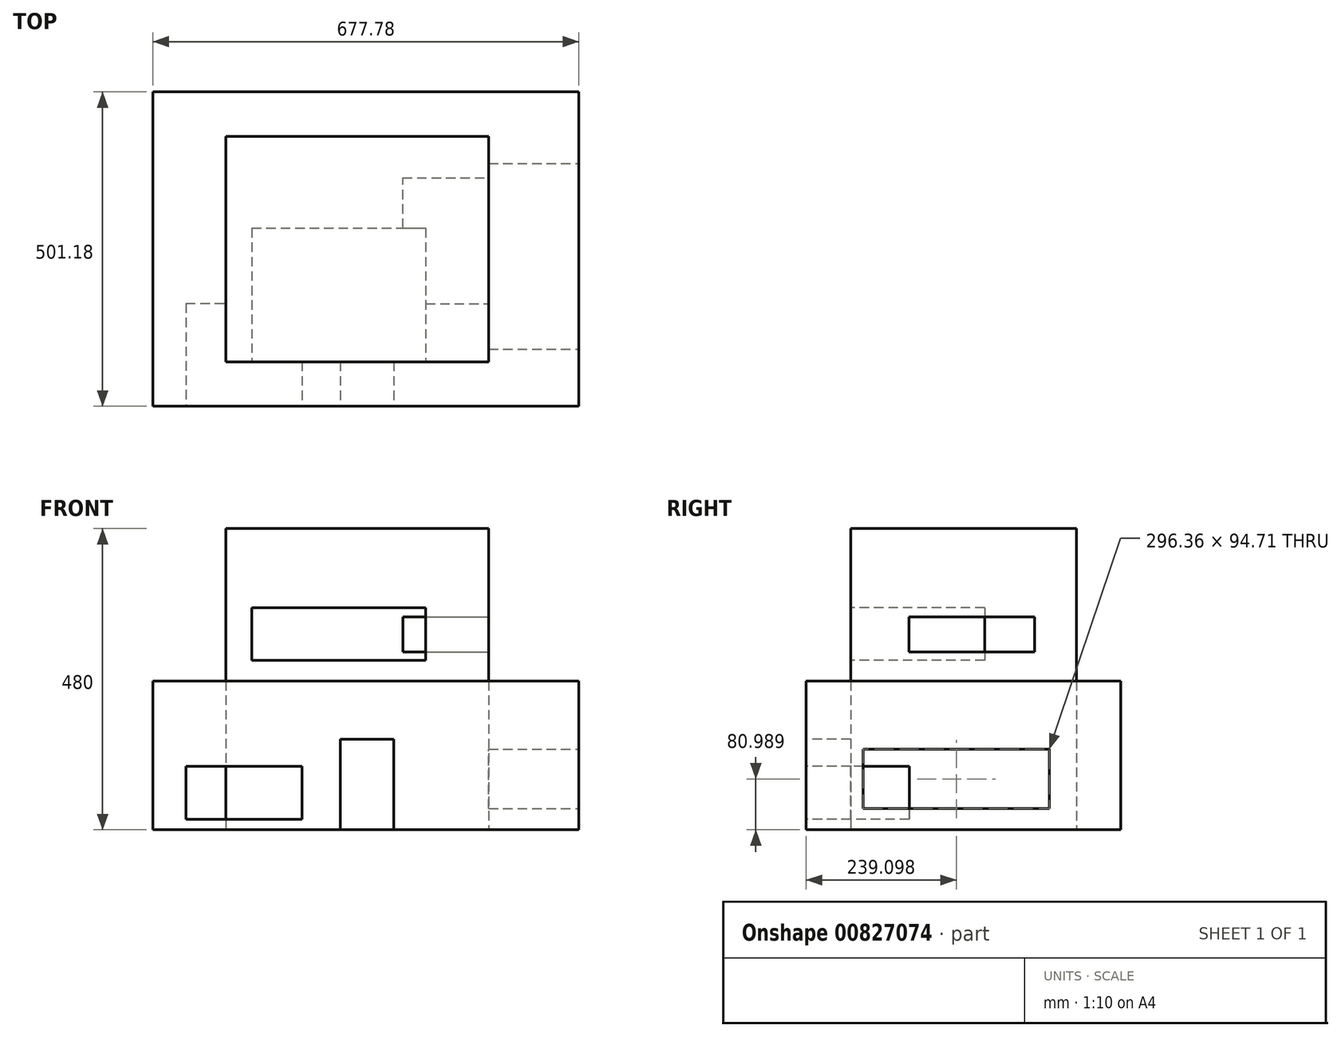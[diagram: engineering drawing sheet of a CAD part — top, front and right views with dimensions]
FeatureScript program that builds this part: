
annotation { "Feature Type Name" : "Feature", "Feature Type Description" : "" }
export const myFeature = defineFeature(function(context is Context, id is Id, definition is map)
    precondition{}
    {
        {
            var Q0;
            Q0=qCreatedBy(makeId("Top.planeOp"),FACE);
            var sketch = newSketch(context, id + "F0", { "sketchPlane" : qUnion([Q0])});
            skLineSegment(sketch, "E0.bottom", {"start": v(-325.29, 250.6) * mm, "end": v(352.5, 250.6) * mm});
            skLineSegment(sketch, "E0.top", {"start": v(-325.29, -250.6) * mm, "end": v(352.5, -250.6) * mm});
            skLineSegment(sketch, "E0.left", {"start": v(-325.29, 250.6) * mm, "end": v(-325.29, -250.6) * mm});
            skLineSegment(sketch, "E0.right", {"start": v(352.5, 250.6) * mm, "end": v(352.5, -250.6) * mm});
            skPoint(sketch, "E0.middle", {"position": v(13.6, 0) * mm});
            skLineSegment(sketch, "E1.bottom", {"start": v(-209.43, -179.54) * mm, "end": v(209.43, -179.54) * mm});
            skLineSegment(sketch, "E1.top", {"start": v(-209.43, 179.54) * mm, "end": v(209.43, 179.54) * mm});
            skLineSegment(sketch, "E1.left", {"start": v(-209.43, -179.54) * mm, "end": v(-209.43, 179.54) * mm});
            skLineSegment(sketch, "E1.right", {"start": v(209.43, -179.54) * mm, "end": v(209.43, 179.54) * mm});
            skPoint(sketch, "E1.middle", {"position": v(0, 0) * mm});
            skSolve(sketch);
        }
        {
            var Q0;
            Q0 = qSketchRegion(id + "F0", true);
            extrude(context, id + "F1", {"entities" : qUnion([Q0]), "depth" : 237 * mm, "offsetDistance" : 25 * mm});
        }
        {
            var Q0;
            Q0=makeQuery(id+"F1.opExtrude","SWEPT_FACE",FACE,{"disambiguationData":[OSD([sQuery(id+"F0.wireOp",EDGE,"E0.top")])]});
            var sketch = newSketch(context, id + "F2", { "sketchPlane" : qUnion([Q0])});
            skLineSegment(sketch, "E2.bottom", {"start": v(-27.2, 0) * mm, "end": v(57.87, 0) * mm});
            skLineSegment(sketch, "E2.top", {"start": v(-27.2, 144.13) * mm, "end": v(57.87, 144.13) * mm});
            skLineSegment(sketch, "E2.left", {"start": v(-27.2, 0) * mm, "end": v(-27.2, 144.13) * mm});
            skLineSegment(sketch, "E2.right", {"start": v(57.87, 0) * mm, "end": v(57.87, 144.13) * mm});
            skLineSegment(sketch, "E3.bottom", {"start": v(-272.79, 101.18) * mm, "end": v(-87.56, 101.18) * mm});
            skLineSegment(sketch, "E3.top", {"start": v(-272.79, 16.75) * mm, "end": v(-87.56, 16.75) * mm});
            skLineSegment(sketch, "E3.left", {"start": v(-272.79, 101.18) * mm, "end": v(-272.79, 16.75) * mm});
            skLineSegment(sketch, "E3.right", {"start": v(-87.56, 101.18) * mm, "end": v(-87.56, 16.75) * mm});
            skSolve(sketch);
        }
        {
            var Q0;
            Q0=makeQuery(id+"F2.imprint","IMPRINT",FACE,{"disambiguationData":[TD([[makeQuery(id+"F2.imprint","IMPRINT",EDGE,{"derivedFrom":sQuery(id+"F2.wireOp",EDGE,"E2.bottom")}),1.0]])]});
            extrude(context, id + "F3", {"entities" : qUnion([Q0]), "operationType" : NewBodyOperationType.REMOVE, "oppositeDirection" : true, "depth" : 154 * mm, "offsetDistance" : 25 * mm});
        }
        {
            var Q0;
            Q0 = qSketchRegion(id + "F2", true);
            extrude(context, id + "F4", {"entities" : qUnion([Q0]), "operationType" : NewBodyOperationType.REMOVE, "oppositeDirection" : true, "depth" : 25 * mm, "offsetDistance" : 25 * mm});
        }
        {
            var Q0;
            Q0=makeQuery(id+"F1.opExtrude","SWEPT_FACE",FACE,{"disambiguationData":[OSD([sQuery(id+"F0.wireOp",EDGE,"E0.right")])]});
            var sketch = newSketch(context, id + "F5", { "sketchPlane" : qUnion([Q0])});
            skLineSegment(sketch, "E4.bottom", {"start": v(-159.67, 128.34) * mm, "end": v(136.69, 128.34) * mm});
            skLineSegment(sketch, "E4.top", {"start": v(-159.67, 33.63) * mm, "end": v(136.69, 33.63) * mm});
            skLineSegment(sketch, "E4.left", {"start": v(-159.67, 128.34) * mm, "end": v(-159.67, 33.63) * mm});
            skLineSegment(sketch, "E4.right", {"start": v(136.69, 128.34) * mm, "end": v(136.69, 33.63) * mm});
            skSolve(sketch);
        }
        {
            var Q0;
            Q0 = qSketchRegion(id + "F5", true);
            extrude(context, id + "F6", {"entities" : qUnion([Q0]), "operationType" : NewBodyOperationType.REMOVE, "oppositeDirection" : true, "depth" : 381 * mm, "offsetDistance" : 25 * mm});
        }
        {
            var Q0;
            Q0=makeQuery(id+"F4.boolean.opBoolean","COPY",FACE,{"derivedFrom":makeQuery(id+"F4.opExtrude","CAP_FACE",FACE,{"disambiguationData":[OSD([sQuery(id+"F2.wireOp",EDGE,"E3.bottom"),sQuery(id+"F2.wireOp",EDGE,"E3.top"),sQuery(id+"F2.wireOp",EDGE,"E3.left"),sQuery(id+"F2.wireOp",EDGE,"E3.right")])],"isStart":false})});
            extrude(context, id + "F7", {"entities" : qUnion([Q0]), "operationType" : NewBodyOperationType.REMOVE, "oppositeDirection" : true, "depth" : 139 * mm, "offsetDistance" : 25 * mm});
        }
        {
            var Q0;
            Q0=makeQuery(id+"F1.opExtrude","CAP_FACE",FACE,{"disambiguationData":[OSD([sQuery(id+"F0.wireOp",EDGE,"E0.bottom"),sQuery(id+"F0.wireOp",EDGE,"E0.top"),sQuery(id+"F0.wireOp",EDGE,"E0.left"),sQuery(id+"F0.wireOp",EDGE,"E0.right"),sQuery(id+"F0.wireOp",EDGE,"E1.bottom"),sQuery(id+"F0.wireOp",EDGE,"E1.top"),sQuery(id+"F0.wireOp",EDGE,"E1.left"),sQuery(id+"F0.wireOp",EDGE,"E1.right")])],"isStart":false});
            var sketch = newSketch(context, id + "F8", { "sketchPlane" : qUnion([Q0])});
            skLineSegment(sketch, "E5.bottom", {"start": v(209.43, 179.54) * mm, "end": v(-209.43, 179.54) * mm});
            skLineSegment(sketch, "E5.top", {"start": v(209.43, -179.54) * mm, "end": v(-209.43, -179.54) * mm});
            skLineSegment(sketch, "E5.left", {"start": v(209.43, 179.54) * mm, "end": v(209.43, -179.54) * mm});
            skLineSegment(sketch, "E5.right", {"start": v(-209.43, 179.54) * mm, "end": v(-209.43, -179.54) * mm});
            skPoint(sketch, "E5.middle", {"position": v(0, 0) * mm});
            skSolve(sketch);
        }
        {
            var Q0;
            Q0 = qSketchRegion(id + "F8", true);
            extrude(context, id + "F9", {"entities" : qUnion([Q0]), "depth" : 243 * mm, "offsetDistance" : 25 * mm});
        }
        {
            var Q0;
            Q0=makeQuery(id+"F9.opExtrude","SWEPT_FACE",FACE,{"disambiguationData":[OSD([sQuery(id+"F8.wireOp",EDGE,"E5.top")])]});
            var sketch = newSketch(context, id + "F10", { "sketchPlane" : qUnion([Q0])});
            skLineSegment(sketch, "E6.bottom", {"start": v(-167.71, 354.2) * mm, "end": v(109.18, 354.2) * mm});
            skLineSegment(sketch, "E6.top", {"start": v(-167.71, 270.33) * mm, "end": v(109.18, 270.33) * mm});
            skLineSegment(sketch, "E6.left", {"start": v(-167.71, 354.2) * mm, "end": v(-167.71, 270.33) * mm});
            skLineSegment(sketch, "E6.right", {"start": v(109.18, 354.2) * mm, "end": v(109.18, 270.33) * mm});
            skSolve(sketch);
        }
        {
            var Q0;
            Q0 = qSketchRegion(id + "F10", true);
            extrude(context, id + "F11", {"entities" : qUnion([Q0]), "operationType" : NewBodyOperationType.REMOVE, "oppositeDirection" : true, "depth" : 213 * mm, "offsetDistance" : 25 * mm});
        }
        {
            var Q0;
            Q0=makeQuery(id+"F9.opExtrude","SWEPT_FACE",FACE,{"disambiguationData":[OSD([sQuery(id+"F8.wireOp",EDGE,"E5.left")])]});
            var sketch = newSketch(context, id + "F12", { "sketchPlane" : qUnion([Q0])});
            skLineSegment(sketch, "E7.bottom", {"start": v(-86.85, 339.05) * mm, "end": v(113.23, 339.05) * mm});
            skLineSegment(sketch, "E7.top", {"start": v(-86.85, 283.62) * mm, "end": v(113.23, 283.62) * mm});
            skLineSegment(sketch, "E7.left", {"start": v(-86.85, 339.05) * mm, "end": v(-86.85, 283.62) * mm});
            skLineSegment(sketch, "E7.right", {"start": v(113.23, 339.05) * mm, "end": v(113.23, 283.62) * mm});
            skSolve(sketch);
        }
        {
            var Q0;
            Q0 = qSketchRegion(id + "F12", true);
            extrude(context, id + "F13", {"entities" : qUnion([Q0]), "operationType" : NewBodyOperationType.REMOVE, "oppositeDirection" : true, "depth" : 137 * mm, "offsetDistance" : 25 * mm});
        }
    });
